# Revit family: IS_IdealRain_A5689_BIM_GB
name_source: partatom
category: Plumbing Fixtures
revit_build: Autodesk Revit MEP 2012 (Build: 20110309_2315(x64)
units: mm (PartAtom-declared; Revit-internal decimal feet)

## types (1)
- A5689AA - Idealrain Dual Shower Kit Round
    Accessories = www.idealspec.co.uk
    AreaUnits = millimeters
    Assembly Code = C1030200
    AssetType = Fixed
    BIMObjectName = ISI_IdealStandard_ShowerMixers_IdealRain_A5689
    BREEAMApproved = No
    Brand = Ideal Standard
    CWFU = 0
    Color = Chrome
    ConnectionType = Plumbing
    Cost = 0 $
    Default Elevation = 1219 mm
    Description = Idealrain Dual Shower Kit Round
    DurationUnit = year
    ECA = No
    ExpectedLife = 30
    FaucetFunction = MIXED
    FaucetOperation = OTHER
    FaucetType = OTHER
    Features = Fixed round head and removable handset
    Finish = Chrome
    HWFU = 0
    ISthermostatic = No
    IfcExportAs = IfcValveType
    IfcExportType = FAUCET
    InstallationInstructions = www.idealspec.co.uk/resources.html
    LinearUnits = millimeters
    ManufacturerURL = www.idealspec.co.uk
    Material = Brass
    Model = A5689AA
    ModelNumber = A5689AA
    ModelReference = Idealrain Dual Shower Kit Round
    NBSDescription = Shower mixers
    NBSReference = 45-35-70/335
    Name = ShowerMixers_IdealRain-A5689_IdealStandard
    NettWeight = 5 Kg
    NominalHeight = 1051 mm  [stored 3.44816 ft]
    NominalLength = 400 mm  [stored 1.31234 ft]
    NominalWidth = 200 mm  [stored 0.656168 ft]
    ProductInformation = www.idealspec.co.uk/assets/datasheet/A5689AA
    ShowerBody = ASH_ArmitageShanks_TapBody_Silver_render
    Size = 1252 x 312 x 488 mm
    Space = Internal
    SpareParts = www.fastpart-spares.co.uk
    TestPressure = 10 Bar
    URL = www.idealspec.co.uk
    Uniclass2 = Pr_40_20_87_81
    Version = 2
    VolumeUnits = Litres
    WFU = 0
    WRAS = No
    WarrantyDescription = Manufacturers Warranty
    WarrantyDurationParts = 5
    WarrantyDurationUnit = year
    WaterEfficientProduct = Yes

note: [stored X ft] marks values corroborated as IEEE doubles in the binary element streams (Revit-internal decimal feet)

## geometry (parser evidence)
native form markers: Sweep x6
no freeform markers — native parametric forms only
